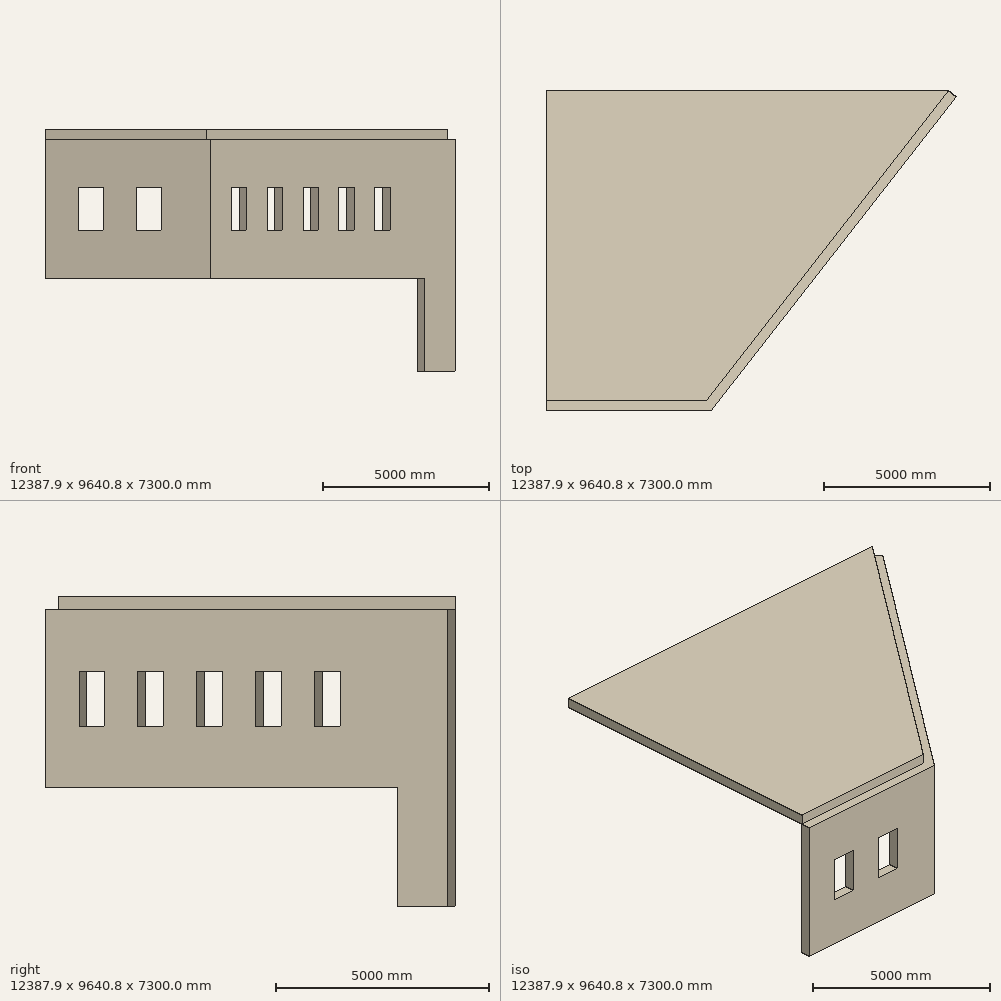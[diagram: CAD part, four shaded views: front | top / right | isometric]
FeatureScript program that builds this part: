
annotation { "Feature Type Name" : "Feature", "Feature Type Description" : "" }
export const myFeature = defineFeature(function(context is Context, id is Id, definition is map)
    precondition{}
    {
        {
            var Q0;
            Q0=qCreatedBy(makeId("Top.planeOp"),FACE);
            var sketch = newSketch(context, id + "F0", { "sketchPlane" : qUnion([Q0])});
            skLineSegment(sketch, "E0", {"start": v(0, 0) * mm, "end": v(5000, 0) * mm});
            skLineSegment(sketch, "E1", {"start": v(5000, 0) * mm, "end": v(12387.94, 9456.13) * mm});
            skLineSegment(sketch, "E2", {"start": v(0, 300) * mm, "end": v(0, 0) * mm});
            skLineSegment(sketch, "E3.0", {"start": v(4853.68, 300) * mm, "end": v(12151.53, 9640.83) * mm});
            skLineSegment(sketch, "E4.0", {"start": v(0, 300) * mm, "end": v(4853.68, 300) * mm});
            skLineSegment(sketch, "E5", {"start": v(12151.53, 9640.83) * mm, "end": v(12387.94, 9456.13) * mm});
            skSolve(sketch);
        }
        {
            var Q0;
            Q0=makeQuery(id+"F0.imprint","IMPRINT",FACE,{"disambiguationData":[TD([[makeQuery(id+"F0.imprint","IMPRINT",EDGE,{"derivedFrom":sQuery(id+"F0.wireOp",EDGE,"E0")}),1.0]])]});
            extrude(context, id + "F1", {"entities" : qUnion([Q0]), "depth" : 7000 * mm});
        }
        {
            var Q0;
            Q0=makeQuery(id+"F1.opExtrude","SWEPT_FACE",FACE,{"disambiguationData":[OSD([sQuery(id+"F0.wireOp",EDGE,"E0")])]});
            var sketch = newSketch(context, id + "F2", { "sketchPlane" : qUnion([Q0])});
            skLineSegment(sketch, "E6.bottom", {"start": v(1000, 5540) * mm, "end": v(1760, 5540) * mm});
            skLineSegment(sketch, "E6.top", {"start": v(1000, 4240) * mm, "end": v(1760, 4240) * mm});
            skLineSegment(sketch, "E6.left", {"start": v(1000, 5540) * mm, "end": v(1000, 4240) * mm});
            skLineSegment(sketch, "E6.right", {"start": v(1760, 5540) * mm, "end": v(1760, 4240) * mm});
            skLineSegment(sketch, "E7.bottom", {"start": v(2760, 5540) * mm, "end": v(3520, 5540) * mm});
            skLineSegment(sketch, "E7.top", {"start": v(2760, 4240) * mm, "end": v(3520, 4240) * mm});
            skLineSegment(sketch, "E7.left", {"start": v(2760, 5540) * mm, "end": v(2760, 4240) * mm});
            skLineSegment(sketch, "E7.right", {"start": v(3520, 5540) * mm, "end": v(3520, 4240) * mm});
            skSolve(sketch);
        }
        {
            var Q0;
            Q0 = qSketchRegion(id + "F2", true);
            extrude(context, id + "F3", {"entities" : qUnion([Q0]), "operationType" : NewBodyOperationType.REMOVE, "endBound" : BoundingType.THROUGH_ALL, "oppositeDirection" : true, "depth" : 25 * mm});
        }
        {
            var Q0;
            Q0=makeQuery(id+"F1.opExtrude","SWEPT_FACE",FACE,{"disambiguationData":[OSD([sQuery(id+"F0.wireOp",EDGE,"E0")])]});
            var sketch = newSketch(context, id + "F4", { "sketchPlane" : qUnion([Q0])});
            skLineSegment(sketch, "E8.bottom", {"start": v(0, 0) * mm, "end": v(5000, 0) * mm});
            skLineSegment(sketch, "E8.top", {"start": v(0, 2800) * mm, "end": v(5000, 2800) * mm});
            skLineSegment(sketch, "E8.left", {"start": v(0, 0) * mm, "end": v(0, 2800) * mm});
            skLineSegment(sketch, "E8.right", {"start": v(5000, 0) * mm, "end": v(5000, 2800) * mm});
            skSolve(sketch);
        }
        {
            var Q0;
            Q0=makeQuery(id+"F4.imprint","IMPRINT",FACE,{"disambiguationData":[TD([[makeQuery(id+"F4.imprint","IMPRINT",EDGE,{"derivedFrom":sQuery(id+"F4.wireOp",EDGE,"E8.bottom")}),1.0]])]});
            extrude(context, id + "F5", {"entities" : qUnion([Q0]), "operationType" : NewBodyOperationType.REMOVE, "endBound" : BoundingType.THROUGH_ALL, "oppositeDirection" : true, "depth" : 25 * mm});
        }
        {
            var Q0;
            Q0=makeQuery(id+"F1.opExtrude","SWEPT_FACE",FACE,{"disambiguationData":[OSD([sQuery(id+"F0.wireOp",EDGE,"E1")])]});
            var sketch = newSketch(context, id + "F6", { "sketchPlane" : qUnion([Q0])});
            skLineSegment(sketch, "E9.bottom", {"start": v(3078.3, 0) * mm, "end": v(13578.3, 0) * mm});
            skLineSegment(sketch, "E9.top", {"start": v(3078.3, 2800) * mm, "end": v(13578.3, 2800) * mm});
            skLineSegment(sketch, "E9.left", {"start": v(3078.3, 0) * mm, "end": v(3078.3, 2800) * mm});
            skLineSegment(sketch, "E9.right", {"start": v(13578.3, 0) * mm, "end": v(13578.3, 2800) * mm});
            skSolve(sketch);
        }
        {
            var Q0;
            Q0 = qSketchRegion(id + "F6", true);
            extrude(context, id + "F7", {"entities" : qUnion([Q0]), "operationType" : NewBodyOperationType.REMOVE, "endBound" : BoundingType.THROUGH_ALL, "oppositeDirection" : true, "depth" : 25 * mm});
        }
        {
            var Q0;
            Q0=makeQuery(id+"F1.opExtrude","SWEPT_FACE",FACE,{"disambiguationData":[OSD([sQuery(id+"F0.wireOp",EDGE,"E1")])]});
            var sketch = newSketch(context, id + "F8", { "sketchPlane" : qUnion([Q0])});
            skLineSegment(sketch, "E10.bottom", {"start": v(4078.3, 5540) * mm, "end": v(4838.3, 5540) * mm});
            skLineSegment(sketch, "E10.top", {"start": v(4078.3, 4240) * mm, "end": v(4838.3, 4240) * mm});
            skLineSegment(sketch, "E10.left", {"start": v(4078.3, 5540) * mm, "end": v(4078.3, 4240) * mm});
            skLineSegment(sketch, "E10.right", {"start": v(4838.3, 5540) * mm, "end": v(4838.3, 4240) * mm});
            skLineSegment(sketch, "E11.bottom", {"start": v(5838.3, 5540) * mm, "end": v(6598.3, 5540) * mm});
            skLineSegment(sketch, "E11.top", {"start": v(5838.3, 4240) * mm, "end": v(6598.3, 4240) * mm});
            skLineSegment(sketch, "E11.left", {"start": v(5838.3, 5540) * mm, "end": v(5838.3, 4240) * mm});
            skLineSegment(sketch, "E11.right", {"start": v(6598.3, 5540) * mm, "end": v(6598.3, 4240) * mm});
            skLineSegment(sketch, "E12.bottom", {"start": v(7598.3, 5540) * mm, "end": v(8358.3, 5540) * mm});
            skLineSegment(sketch, "E12.top", {"start": v(7598.3, 4240) * mm, "end": v(8358.3, 4240) * mm});
            skLineSegment(sketch, "E12.left", {"start": v(7598.3, 5540) * mm, "end": v(7598.3, 4240) * mm});
            skLineSegment(sketch, "E12.right", {"start": v(8358.3, 5540) * mm, "end": v(8358.3, 4240) * mm});
            skLineSegment(sketch, "E13.bottom", {"start": v(9358.3, 5540) * mm, "end": v(10118.3, 5540) * mm});
            skLineSegment(sketch, "E13.top", {"start": v(9358.3, 4240) * mm, "end": v(10118.3, 4240) * mm});
            skLineSegment(sketch, "E13.left", {"start": v(9358.3, 5540) * mm, "end": v(9358.3, 4240) * mm});
            skLineSegment(sketch, "E13.right", {"start": v(10118.3, 5540) * mm, "end": v(10118.3, 4240) * mm});
            skLineSegment(sketch, "E14.bottom", {"start": v(11118.3, 5540) * mm, "end": v(11878.3, 5540) * mm});
            skLineSegment(sketch, "E14.top", {"start": v(11118.3, 4240) * mm, "end": v(11878.3, 4240) * mm});
            skLineSegment(sketch, "E14.left", {"start": v(11118.3, 5540) * mm, "end": v(11118.3, 4240) * mm});
            skLineSegment(sketch, "E14.right", {"start": v(11878.3, 5540) * mm, "end": v(11878.3, 4240) * mm});
            skSolve(sketch);
        }
        {
            var Q0;
            Q0 = qSketchRegion(id + "F8", true);
            extrude(context, id + "F9", {"entities" : qUnion([Q0]), "operationType" : NewBodyOperationType.REMOVE, "endBound" : BoundingType.THROUGH_ALL, "oppositeDirection" : true, "depth" : 25 * mm});
        }
        {
            var Q0;
            Q0=makeQuery(id+"F1.opExtrude","CAP_FACE",FACE,{"disambiguationData":[OSD([sQuery(id+"F0.wireOp",EDGE,"E0"),sQuery(id+"F0.wireOp",EDGE,"E1"),sQuery(id+"F0.wireOp",EDGE,"E2"),sQuery(id+"F0.wireOp",EDGE,"E3.0"),sQuery(id+"F0.wireOp",EDGE,"E4.0"),sQuery(id+"F0.wireOp",EDGE,"E5")])],"isStart":false});
            var sketch = newSketch(context, id + "F10", { "sketchPlane" : qUnion([Q0])});
            skLineSegment(sketch, "E15", {"start": v(0, 300) * mm, "end": v(0, 9640.83) * mm});
            skLineSegment(sketch, "E16", {"start": v(0, 9640.83) * mm, "end": v(12151.53, 9640.83) * mm});
            skSolve(sketch);
        }
        {
            var Q0;
            Q0=makeQuery(id+"F10.imprint","IMPRINT",FACE,{"disambiguationData":[TD([[makeQuery(id+"F10.imprint","IMPRINT",EDGE,{"derivedFrom":sQuery(id+"F10.wireOp",EDGE,"E15")}),-1.0]])]});
            extrude(context, id + "F11", {"entities" : qUnion([Q0]), "depth" : 300 * mm});
        }
    });
